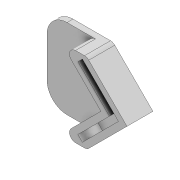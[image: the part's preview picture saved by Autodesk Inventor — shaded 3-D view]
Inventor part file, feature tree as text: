
AUTODESK INVENTOR PART (.ipt)
format: ipt  version: 2022 (Build 260153000, 153)  size: 140,288 bytes
history: native  units: mm
features: extrude x2, fillet x2, other x1, sketch x1
ambient origin geometry x8: Origin, YZ Plane, XZ Plane, XY Plane, X Axis, Y Axis, Z Axis, Center Point
bodies: Body1 (feature_tree)
feature tree (6):
  other  "Sólido1"
  extrude  "Extrusión1"  Depth=40.0mm
  extrude  "Extrusión2"  TaperAngle=90.0deg  [1 undecoded]
  fillet  "Empalme1"  Radius=3.0mm
  fillet  "Empalme2"  Radius=3.0mm
  sketch  "Boceto2"  dims[d0=30.0mm d1=40.0mm d2=90.0deg d10=3.0mm d11=0.0mm d12=3.0mm d13=3.2mm d14=3.0mm d15=25.5mm d16=25.5mm d17=180.0deg d18=180.0deg d19=3.0mm d20=3.0mm d21=3.0mm d22=3.2mm d23=10.0mm d24=0.0mm d31=3.0mm d32=10.0mm d25=0.0mm d26=0.0mm d27=0.0mm d28=0.0mm]
note: 1 required parameter value undecoded (feature->parameter linkage not recoverable at this tier; creation-order binding heuristic only, values carry confidence <= 0.55)
